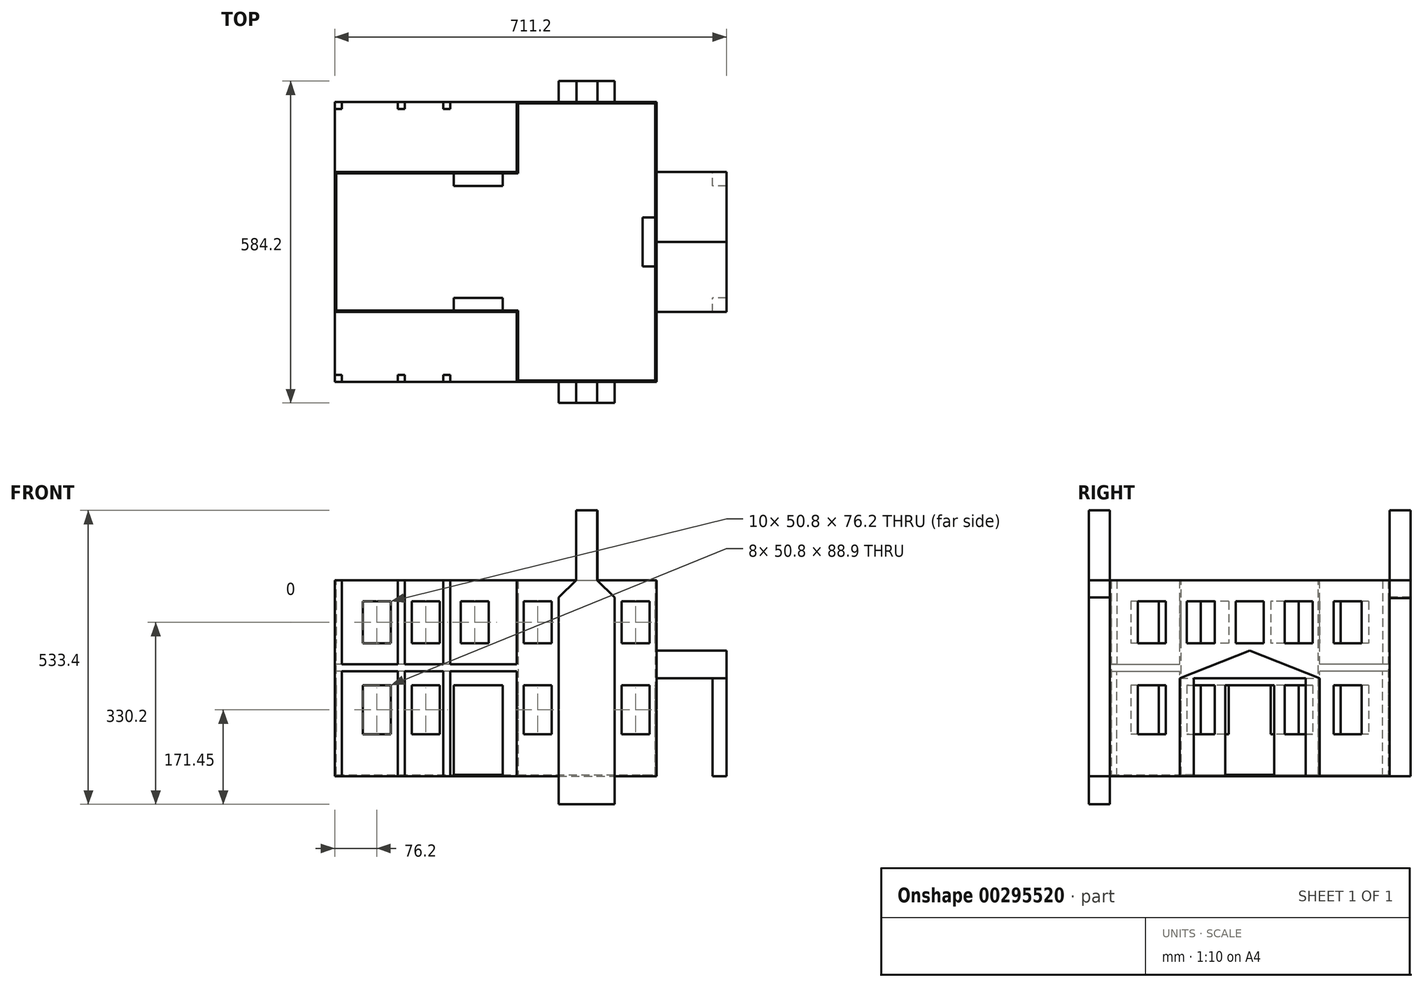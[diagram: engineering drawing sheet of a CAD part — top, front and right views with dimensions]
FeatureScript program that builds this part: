
annotation { "Feature Type Name" : "Feature", "Feature Type Description" : "" }
export const myFeature = defineFeature(function(context is Context, id is Id, definition is map)
    precondition{}
    {
        {
            var Q0;
            Q0=qCreatedBy(makeId("Top.planeOp"),FACE);
            var sketch = newSketch(context, id + "F0", { "sketchPlane" : qUnion([Q0])});
            skLineSegment(sketch, "E0.bottom", {"start": v(0, 0) * mm, "end": v(254, 0) * mm});
            skLineSegment(sketch, "E0.top", {"start": v(0, 508) * mm, "end": v(254, 508) * mm});
            skLineSegment(sketch, "E0.left", {"start": v(0, 0) * mm, "end": v(0, 508) * mm});
            skLineSegment(sketch, "E0.right", {"start": v(254, 0) * mm, "end": v(254, 508) * mm});
            skSolve(sketch);
        }
        {
            var Q0;
            Q0 = qSketchRegion(id + "F0", true);
            extrude(context, id + "F1", {"entities" : qUnion([Q0]), "depth" : 355.6 * mm});
        }
        {
            var Q0;
            Q0=makeQuery(id+"F1.opExtrude","SWEPT_FACE",FACE,{"disambiguationData":[OSD([sQuery(id+"F0.wireOp",EDGE,"E0.left")])]});
            var sketch = newSketch(context, id + "F2", { "sketchPlane" : qUnion([Q0])});
            skLineSegment(sketch, "E1.bottom", {"start": v(-381, 0) * mm, "end": v(-127, 0) * mm});
            skLineSegment(sketch, "E1.top", {"start": v(-381, 355.6) * mm, "end": v(-127, 355.6) * mm});
            skLineSegment(sketch, "E1.left", {"start": v(-381, 0) * mm, "end": v(-381, 355.6) * mm});
            skLineSegment(sketch, "E1.right", {"start": v(-127, 0) * mm, "end": v(-127, 355.6) * mm});
            skSolve(sketch);
        }
        {
            var Q0;
            Q0 = qSketchRegion(id + "F2", true);
            extrude(context, id + "F3", {"entities" : qUnion([Q0]), "operationType" : NewBodyOperationType.ADD, "depth" : 330.2 * mm});
        }
        {
            var Q0;
            Q0=makeQuery(id+"F3.boolean.opBoolean","MERGE",FACE,{"derivedFrom":[makeQuery(id+"F1.opExtrude","CAP_FACE",FACE,{"disambiguationData":[OSD([sQuery(id+"F0.wireOp",EDGE,"E0.bottom"),sQuery(id+"F0.wireOp",EDGE,"E0.top"),sQuery(id+"F0.wireOp",EDGE,"E0.left"),sQuery(id+"F0.wireOp",EDGE,"E0.right")])],"isStart":false}),makeQuery(id+"F3.opExtrude","SWEPT_FACE",FACE,{"disambiguationData":[OSD([sQuery(id+"F2.wireOp",EDGE,"E1.top")])]})]});
            shell(context, id + "F4", {"entities" : qUnion([Q0]), "thickness" : 2.54 * mm});
        }
        {
            var Q0;
            Q0=makeQuery(id+"F1.opExtrude","SWEPT_FACE",FACE,{"disambiguationData":[OSD([sQuery(id+"F0.wireOp",EDGE,"E0.right")])]});
            var sketch = newSketch(context, id + "F5", { "sketchPlane" : qUnion([Q0])});
            skLineSegment(sketch, "E2.bottom", {"start": v(50.8, 317.5) * mm, "end": v(101.6, 317.5) * mm});
            skLineSegment(sketch, "E2.top", {"start": v(50.8, 241.3) * mm, "end": v(101.6, 241.3) * mm});
            skLineSegment(sketch, "E2.left", {"start": v(50.8, 317.5) * mm, "end": v(50.8, 241.3) * mm});
            skLineSegment(sketch, "E2.right", {"start": v(101.6, 317.5) * mm, "end": v(101.6, 241.3) * mm});
            skLineSegment(sketch, "E3.bottom", {"start": v(139.7, 317.5) * mm, "end": v(190.5, 317.5) * mm});
            skLineSegment(sketch, "E3.top", {"start": v(139.7, 241.3) * mm, "end": v(190.5, 241.3) * mm});
            skLineSegment(sketch, "E3.left", {"start": v(139.7, 317.5) * mm, "end": v(139.7, 241.3) * mm});
            skLineSegment(sketch, "E3.right", {"start": v(190.5, 317.5) * mm, "end": v(190.5, 241.3) * mm});
            skLineSegment(sketch, "E4.bottom", {"start": v(228.6, 317.5) * mm, "end": v(279.4, 317.5) * mm});
            skLineSegment(sketch, "E4.top", {"start": v(228.6, 241.3) * mm, "end": v(279.4, 241.3) * mm});
            skLineSegment(sketch, "E4.left", {"start": v(228.6, 317.5) * mm, "end": v(228.6, 241.3) * mm});
            skLineSegment(sketch, "E4.right", {"start": v(279.4, 317.5) * mm, "end": v(279.4, 241.3) * mm});
            skLineSegment(sketch, "E5.bottom", {"start": v(317.5, 317.5) * mm, "end": v(368.3, 317.5) * mm});
            skLineSegment(sketch, "E5.top", {"start": v(317.5, 241.3) * mm, "end": v(368.3, 241.3) * mm});
            skLineSegment(sketch, "E5.left", {"start": v(317.5, 317.5) * mm, "end": v(317.5, 241.3) * mm});
            skLineSegment(sketch, "E5.right", {"start": v(368.3, 317.5) * mm, "end": v(368.3, 241.3) * mm});
            skLineSegment(sketch, "E6.bottom", {"start": v(406.4, 317.5) * mm, "end": v(457.2, 317.5) * mm});
            skLineSegment(sketch, "E6.top", {"start": v(406.4, 241.3) * mm, "end": v(457.2, 241.3) * mm});
            skLineSegment(sketch, "E6.left", {"start": v(406.4, 317.5) * mm, "end": v(406.4, 241.3) * mm});
            skLineSegment(sketch, "E6.right", {"start": v(457.2, 317.5) * mm, "end": v(457.2, 241.3) * mm});
            skPoint(sketch, "E7.endSnap0", {"position": v(254, 317.5) * mm});
            skSolve(sketch);
        }
        {
            var Q0;
            Q0 = qSketchRegion(id + "F5", true);
            extrude(context, id + "F6", {"entities" : qUnion([Q0]), "operationType" : NewBodyOperationType.REMOVE, "oppositeDirection" : true, "depth" : 25.4 * mm});
        }
        {
            var Q0;
            Q0=makeQuery(id+"F1.opExtrude","SWEPT_FACE",FACE,{"disambiguationData":[OSD([sQuery(id+"F0.wireOp",EDGE,"E0.right")])]});
            var sketch = newSketch(context, id + "F7", { "sketchPlane" : qUnion([Q0])});
            skLineSegment(sketch, "E8", {"start": v(254, 228.44) * mm, "end": v(381, 177.8) * mm});
            skLineSegment(sketch, "E9", {"start": v(127, 177.8) * mm, "end": v(381, 177.8) * mm});
            skLineSegment(sketch, "E10", {"start": v(127, 177.8) * mm, "end": v(254, 228.44) * mm});
            skSolve(sketch);
        }
        {
            var Q0;
            Q0=makeQuery(id+"F1.opExtrude","SWEPT_FACE",FACE,{"disambiguationData":[OSD([sQuery(id+"F0.wireOp",EDGE,"E0.right")])]});
            var sketch = newSketch(context, id + "F8", { "sketchPlane" : qUnion([Q0])});
            skLineSegment(sketch, "E11.bottom", {"start": v(50.8, 165.1) * mm, "end": v(101.6, 165.1) * mm});
            skLineSegment(sketch, "E11.top", {"start": v(50.8, 76.2) * mm, "end": v(101.6, 76.2) * mm});
            skLineSegment(sketch, "E11.left", {"start": v(50.8, 165.1) * mm, "end": v(50.8, 76.2) * mm});
            skLineSegment(sketch, "E11.right", {"start": v(101.6, 165.1) * mm, "end": v(101.6, 76.2) * mm});
            skLineSegment(sketch, "E12.bottom", {"start": v(139.7, 165.1) * mm, "end": v(190.5, 165.1) * mm});
            skLineSegment(sketch, "E12.top", {"start": v(139.7, 76.2) * mm, "end": v(190.5, 76.2) * mm});
            skLineSegment(sketch, "E12.left", {"start": v(139.7, 165.1) * mm, "end": v(139.7, 76.2) * mm});
            skLineSegment(sketch, "E12.right", {"start": v(190.5, 165.1) * mm, "end": v(190.5, 76.2) * mm});
            skLineSegment(sketch, "E13.bottom", {"start": v(406.4, 165.1) * mm, "end": v(457.2, 165.1) * mm});
            skLineSegment(sketch, "E13.top", {"start": v(406.4, 76.2) * mm, "end": v(457.2, 76.2) * mm});
            skLineSegment(sketch, "E13.left", {"start": v(406.4, 165.1) * mm, "end": v(406.4, 76.2) * mm});
            skLineSegment(sketch, "E13.right", {"start": v(457.2, 165.1) * mm, "end": v(457.2, 76.2) * mm});
            skLineSegment(sketch, "E14.bottom", {"start": v(317.5, 165.1) * mm, "end": v(368.3, 165.1) * mm});
            skLineSegment(sketch, "E14.top", {"start": v(317.5, 76.2) * mm, "end": v(368.3, 76.2) * mm});
            skLineSegment(sketch, "E14.left", {"start": v(317.5, 165.1) * mm, "end": v(317.5, 76.2) * mm});
            skLineSegment(sketch, "E14.right", {"start": v(368.3, 165.1) * mm, "end": v(368.3, 76.2) * mm});
            skLineSegment(sketch, "E15.bottom", {"start": v(209.55, 165.1) * mm, "end": v(298.45, 165.1) * mm});
            skLineSegment(sketch, "E15.top", {"start": v(209.55, 0) * mm, "end": v(298.45, 0) * mm});
            skLineSegment(sketch, "E15.left", {"start": v(209.55, 165.1) * mm, "end": v(209.55, 0) * mm});
            skLineSegment(sketch, "E15.right", {"start": v(298.45, 165.1) * mm, "end": v(298.45, 0) * mm});
            skSolve(sketch);
        }
        {
            var Q0;
            Q0=makeQuery(id+"F7.imprint","IMPRINT",FACE,{"disambiguationData":[TD([[makeQuery(id+"F7.imprint","IMPRINT",EDGE,{"derivedFrom":sQuery(id+"F7.wireOp",EDGE,"E8")}),-1.0]])]});
            extrude(context, id + "F9", {"entities" : qUnion([Q0]), "operationType" : NewBodyOperationType.ADD, "depth" : 127 * mm});
        }
        {
            var Q0;
            Q0=makeQuery(id+"F9.opExtrude","SWEPT_FACE",FACE,{"disambiguationData":[OSD([sQuery(id+"F7.wireOp",EDGE,"E9")])]});
            var sketch = newSketch(context, id + "F10", { "sketchPlane" : qUnion([Q0])});
            skLineSegment(sketch, "E16.bottom", {"start": v(381, -127) * mm, "end": v(355.6, -127) * mm});
            skLineSegment(sketch, "E16.top", {"start": v(381, -152.4) * mm, "end": v(355.6, -152.4) * mm});
            skLineSegment(sketch, "E16.left", {"start": v(381, -127) * mm, "end": v(381, -152.4) * mm});
            skLineSegment(sketch, "E16.right", {"start": v(355.6, -127) * mm, "end": v(355.6, -152.4) * mm});
            skLineSegment(sketch, "E17.bottom", {"start": v(381, -355.6) * mm, "end": v(355.6, -355.6) * mm});
            skLineSegment(sketch, "E17.top", {"start": v(381, -381) * mm, "end": v(355.6, -381) * mm});
            skLineSegment(sketch, "E17.left", {"start": v(381, -355.6) * mm, "end": v(381, -381) * mm});
            skLineSegment(sketch, "E17.right", {"start": v(355.6, -355.6) * mm, "end": v(355.6, -381) * mm});
            skSolve(sketch);
        }
        {
            var Q0;
            Q0=makeQuery(id+"F10.imprint","IMPRINT",FACE,{"disambiguationData":[TD([[makeQuery(id+"F10.imprint","IMPRINT",EDGE,{"derivedFrom":sQuery(id+"F10.wireOp",EDGE,"E16.bottom")}),1.0]])]});
            var Q1;
            Q1=makeQuery(id+"F10.imprint","IMPRINT",FACE,{"disambiguationData":[TD([[makeQuery(id+"F10.imprint","IMPRINT",EDGE,{"derivedFrom":sQuery(id+"F10.wireOp",EDGE,"E17.bottom")}),1.0]])]});
            extrude(context, id + "F11", {"entities" : qUnion([Q0, Q1]), "operationType" : NewBodyOperationType.ADD, "depth" : 177.8 * mm});
        }
        {
            var Q0;
            Q0=makeQuery(id+"F8.imprint","IMPRINT",FACE,{"disambiguationData":[TD([[makeQuery(id+"F8.imprint","IMPRINT",EDGE,{"derivedFrom":sQuery(id+"F8.wireOp",EDGE,"E11.bottom")}),-1.0]])]});
            var Q1;
            Q1=makeQuery(id+"F8.imprint","IMPRINT",FACE,{"disambiguationData":[TD([[makeQuery(id+"F8.imprint","IMPRINT",EDGE,{"derivedFrom":sQuery(id+"F8.wireOp",EDGE,"E12.bottom")}),-1.0]])]});
            var Q2;
            Q2=makeQuery(id+"F8.imprint","IMPRINT",FACE,{"disambiguationData":[TD([[makeQuery(id+"F8.imprint","IMPRINT",EDGE,{"derivedFrom":sQuery(id+"F8.wireOp",EDGE,"E15.bottom")}),-1.0]])]});
            var Q3;
            Q3=makeQuery(id+"F8.imprint","IMPRINT",FACE,{"disambiguationData":[TD([[makeQuery(id+"F8.imprint","IMPRINT",EDGE,{"derivedFrom":sQuery(id+"F8.wireOp",EDGE,"E14.bottom")}),-1.0]])]});
            var Q4;
            Q4=makeQuery(id+"F8.imprint","IMPRINT",FACE,{"disambiguationData":[TD([[makeQuery(id+"F8.imprint","IMPRINT",EDGE,{"derivedFrom":sQuery(id+"F8.wireOp",EDGE,"E13.bottom")}),-1.0]])]});
            extrude(context, id + "F12", {"entities" : qUnion([Q0, Q1, Q2, Q3, Q4]), "operationType" : NewBodyOperationType.REMOVE, "oppositeDirection" : true, "depth" : 25.4 * mm});
        }
        {
            var Q0;
            Q0=makeQuery(id+"F1.opExtrude","SWEPT_FACE",FACE,{"disambiguationData":[OSD([sQuery(id+"F0.wireOp",EDGE,"E0.right")])]});
            var sketch = newSketch(context, id + "F13", { "sketchPlane" : qUnion([Q0])});
            skLineSegment(sketch, "E18.bottom", {"start": v(209.55, 165.1) * mm, "end": v(298.45, 165.1) * mm});
            skLineSegment(sketch, "E18.top", {"start": v(209.55, 0) * mm, "end": v(298.45, 0) * mm});
            skLineSegment(sketch, "E18.left", {"start": v(209.55, 165.1) * mm, "end": v(209.55, 0) * mm});
            skLineSegment(sketch, "E18.right", {"start": v(298.45, 165.1) * mm, "end": v(298.45, 0) * mm});
            skSolve(sketch);
        }
        {
            var Q0;
            Q0=makeQuery(id+"F1.opExtrude","SWEPT_FACE",FACE,{"disambiguationData":[OSD([sQuery(id+"F0.wireOp",EDGE,"E0.bottom")])]});
            var sketch = newSketch(context, id + "F14", { "sketchPlane" : qUnion([Q0])});
            skLineSegment(sketch, "E19", {"start": v(76.2, 0) * mm, "end": v(76.2, 324.5) * mm});
            skLineSegment(sketch, "E20", {"start": v(177.8, 0) * mm, "end": v(177.8, 324.5) * mm});
            skLineSegment(sketch, "E21", {"start": v(76.2, 324.5) * mm, "end": v(107.95, 355.6) * mm});
            skLineSegment(sketch, "E22", {"start": v(177.8, 324.5) * mm, "end": v(146.05, 355.6) * mm});
            skLineSegment(sketch, "E23", {"start": v(146.05, 355.6) * mm, "end": v(146.05, 482.6) * mm});
            skLineSegment(sketch, "E24", {"start": v(107.95, 355.6) * mm, "end": v(107.95, 482.6) * mm});
            skLineSegment(sketch, "E25", {"start": v(107.95, 482.6) * mm, "end": v(146.05, 482.6) * mm});
            skLineSegment(sketch, "E26.top", {"start": v(76.2, -50.8) * mm, "end": v(177.79, -50.8) * mm});
            skLineSegment(sketch, "E26.left", {"start": v(76.2, 0) * mm, "end": v(76.2, -50.8) * mm});
            skLineSegment(sketch, "E26.right", {"start": v(177.79, 0) * mm, "end": v(177.79, -50.8) * mm});
            skSolve(sketch);
        }
        {
            var Q0;
            {var subQ2=sQuery(id+"F14.wireOp",EDGE,"E19");Q0=makeQuery(id+"F14.imprint","IMPRINT",FACE,{"disambiguationData":[TD([[makeQuery(id+"F14.imprint","IMPRINT",EDGE,{"derivedFrom":subQ2}),-1.0]])]});}
            var Q1;
            {var subQ0=sQuery(id+"F14.wireOp",EDGE,"E25");Q1=makeQuery(id+"F14.imprint","IMPRINT",FACE,{"disambiguationData":[TD([[makeQuery(id+"F14.imprint","IMPRINT",EDGE,{"derivedFrom":subQ0}),-1.0]])]});}
            var Q2;
            Q2=makeQuery(id+"F14.imprint","IMPRINT",FACE,{"disambiguationData":[TD([[makeQuery(id+"F14.imprint","IMPRINT",EDGE,{"derivedFrom":sQuery(id+"F14.wireOp",EDGE,"E26.top")}),1.0]])]});
            extrude(context, id + "F15", {"entities" : qUnion([Q0, Q1, Q2]), "operationType" : NewBodyOperationType.ADD, "depth" : 38.1 * mm});
        }
        {
            var Q0;
            Q0=makeQuery(id+"F1.opExtrude","SWEPT_FACE",FACE,{"disambiguationData":[OSD([sQuery(id+"F0.wireOp",EDGE,"E0.top")])]});
            var sketch = newSketch(context, id + "F16", { "sketchPlane" : qUnion([Q0])});
            skLineSegment(sketch, "E27", {"start": v(-177.8, 0) * mm, "end": v(-177.8, 323.73) * mm});
            skLineSegment(sketch, "E28", {"start": v(-177.8, 323.73) * mm, "end": v(-146.8, 355.6) * mm});
            skLineSegment(sketch, "E29", {"start": v(-146.8, 355.6) * mm, "end": v(-146.8, 482.6) * mm});
            skLineSegment(sketch, "E30", {"start": v(-146.8, 482.6) * mm, "end": v(-108.7, 482.6) * mm});
            skLineSegment(sketch, "E31", {"start": v(-108.7, 482.6) * mm, "end": v(-108.7, 355.6) * mm});
            skLineSegment(sketch, "E32", {"start": v(-108.7, 355.6) * mm, "end": v(-76.2, 325.29) * mm});
            skLineSegment(sketch, "E33", {"start": v(-76.2, 325.29) * mm, "end": v(-76.2, 0) * mm});
            skLineSegment(sketch, "E34", {"start": v(-76.2, 0) * mm, "end": v(-177.8, 0) * mm});
            skLineSegment(sketch, "E35.bottom", {"start": v(-177.8, 0) * mm, "end": v(-76.2, 0) * mm});
            skLineSegment(sketch, "E35.top", {"start": v(-177.8, -50.8) * mm, "end": v(-76.2, -50.8) * mm});
            skLineSegment(sketch, "E35.left", {"start": v(-177.8, 0) * mm, "end": v(-177.8, -50.8) * mm});
            skLineSegment(sketch, "E35.right", {"start": v(-76.2, 0) * mm, "end": v(-76.2, -50.8) * mm});
            skSolve(sketch);
        }
        {
            var Q0;
            Q0=makeQuery(id+"F16.imprint","IMPRINT",FACE,{"disambiguationData":[TD([[makeQuery(id+"F16.imprint","IMPRINT",EDGE,{"derivedFrom":sQuery(id+"F16.wireOp",EDGE,"E27")}),-1.0]])]});
            var Q1;
            {var subQ0=sQuery(id+"F16.wireOp",EDGE,"E29");Q1=makeQuery(id+"F16.imprint","IMPRINT",FACE,{"disambiguationData":[TD([[makeQuery(id+"F16.imprint","IMPRINT",EDGE,{"derivedFrom":subQ0}),-1.0]])]});}
            var Q2;
            Q2=makeQuery(id+"F16.imprint","IMPRINT",FACE,{"disambiguationData":[TD([[makeQuery(id+"F16.imprint","IMPRINT",EDGE,{"derivedFrom":sQuery(id+"F16.wireOp",EDGE,"E35.bottom")}),1.0]])]});
            extrude(context, id + "F17", {"entities" : qUnion([Q0, Q1, Q2]), "operationType" : NewBodyOperationType.ADD, "depth" : 38.1 * mm});
        }
        {
            var Q0;
            Q0=makeQuery(id+"F3.opExtrude","SWEPT_FACE",FACE,{"disambiguationData":[OSD([sQuery(id+"F2.wireOp",EDGE,"E1.right")])]});
            var sketch = newSketch(context, id + "F18", { "sketchPlane" : qUnion([Q0])});
            skLineSegment(sketch, "E36.bottom", {"start": v(-279.4, 317.5) * mm, "end": v(-228.6, 317.5) * mm});
            skLineSegment(sketch, "E36.top", {"start": v(-279.4, 241.3) * mm, "end": v(-228.6, 241.3) * mm});
            skLineSegment(sketch, "E36.left", {"start": v(-279.4, 317.5) * mm, "end": v(-279.4, 241.3) * mm});
            skLineSegment(sketch, "E36.right", {"start": v(-228.6, 317.5) * mm, "end": v(-228.6, 241.3) * mm});
            skLineSegment(sketch, "E37.bottom", {"start": v(-190.5, 317.5) * mm, "end": v(-139.7, 317.5) * mm});
            skLineSegment(sketch, "E37.top", {"start": v(-190.5, 241.3) * mm, "end": v(-139.7, 241.3) * mm});
            skLineSegment(sketch, "E37.left", {"start": v(-190.5, 317.5) * mm, "end": v(-190.5, 241.3) * mm});
            skLineSegment(sketch, "E37.right", {"start": v(-139.7, 317.5) * mm, "end": v(-139.7, 241.3) * mm});
            skLineSegment(sketch, "E38.bottom", {"start": v(-101.6, 317.5) * mm, "end": v(-50.8, 317.5) * mm});
            skLineSegment(sketch, "E38.top", {"start": v(-101.6, 241.3) * mm, "end": v(-50.8, 241.3) * mm});
            skLineSegment(sketch, "E38.left", {"start": v(-101.6, 317.5) * mm, "end": v(-101.6, 241.3) * mm});
            skLineSegment(sketch, "E38.right", {"start": v(-50.8, 317.5) * mm, "end": v(-50.8, 241.3) * mm});
            skLineSegment(sketch, "E39.bottom", {"start": v(-279.4, 165.1) * mm, "end": v(-228.6, 165.1) * mm});
            skLineSegment(sketch, "E39.top", {"start": v(-279.4, 76.2) * mm, "end": v(-228.6, 76.2) * mm});
            skLineSegment(sketch, "E39.left", {"start": v(-279.4, 165.1) * mm, "end": v(-279.4, 76.2) * mm});
            skLineSegment(sketch, "E39.right", {"start": v(-228.6, 165.1) * mm, "end": v(-228.6, 76.2) * mm});
            skLineSegment(sketch, "E40.bottom", {"start": v(-190.5, 165.1) * mm, "end": v(-139.7, 165.1) * mm});
            skLineSegment(sketch, "E40.top", {"start": v(-190.5, 76.2) * mm, "end": v(-139.7, 76.2) * mm});
            skLineSegment(sketch, "E40.left", {"start": v(-190.5, 165.1) * mm, "end": v(-190.5, 76.2) * mm});
            skLineSegment(sketch, "E40.right", {"start": v(-139.7, 165.1) * mm, "end": v(-139.7, 76.2) * mm});
            skSolve(sketch);
        }
        {
            var Q0;
            Q0=makeQuery(id+"F18.imprint","IMPRINT",FACE,{"disambiguationData":[TD([[makeQuery(id+"F18.imprint","IMPRINT",EDGE,{"derivedFrom":sQuery(id+"F18.wireOp",EDGE,"E36.bottom")}),-1.0]])]});
            var Q1;
            Q1=makeQuery(id+"F18.imprint","IMPRINT",FACE,{"disambiguationData":[TD([[makeQuery(id+"F18.imprint","IMPRINT",EDGE,{"derivedFrom":sQuery(id+"F18.wireOp",EDGE,"E37.bottom")}),-1.0]])]});
            var Q2;
            Q2=makeQuery(id+"F18.imprint","IMPRINT",FACE,{"disambiguationData":[TD([[makeQuery(id+"F18.imprint","IMPRINT",EDGE,{"derivedFrom":sQuery(id+"F18.wireOp",EDGE,"E38.bottom")}),-1.0]])]});
            var Q3;
            Q3=makeQuery(id+"F18.imprint","IMPRINT",FACE,{"disambiguationData":[TD([[makeQuery(id+"F18.imprint","IMPRINT",EDGE,{"derivedFrom":sQuery(id+"F18.wireOp",EDGE,"E40.bottom")}),-1.0]])]});
            var Q4;
            Q4=makeQuery(id+"F18.imprint","IMPRINT",FACE,{"disambiguationData":[TD([[makeQuery(id+"F18.imprint","IMPRINT",EDGE,{"derivedFrom":sQuery(id+"F18.wireOp",EDGE,"E39.bottom")}),-1.0]])]});
            extrude(context, id + "F19", {"entities" : qUnion([Q0, Q1, Q2, Q3, Q4]), "operationType" : NewBodyOperationType.REMOVE, "oppositeDirection" : true, "depth" : 25.4 * mm});
        }
        {
            var Q0;
            Q0=makeQuery(id+"F3.opExtrude","SWEPT_FACE",FACE,{"disambiguationData":[OSD([sQuery(id+"F2.wireOp",EDGE,"E1.right")])]});
            var sketch = newSketch(context, id + "F20", { "sketchPlane" : qUnion([Q0])});
            skLineSegment(sketch, "E41.bottom", {"start": v(-114.3, 165.1) * mm, "end": v(-25.4, 165.1) * mm});
            skLineSegment(sketch, "E41.top", {"start": v(-114.3, 0) * mm, "end": v(-25.4, 0) * mm});
            skLineSegment(sketch, "E41.left", {"start": v(-114.3, 165.1) * mm, "end": v(-114.3, 0) * mm});
            skLineSegment(sketch, "E41.right", {"start": v(-25.4, 165.1) * mm, "end": v(-25.4, 0) * mm});
            skSolve(sketch);
        }
        {
            var Q0;
            Q0=makeQuery(id+"F20.imprint","IMPRINT",FACE,{"disambiguationData":[TD([[makeQuery(id+"F20.imprint","IMPRINT",EDGE,{"derivedFrom":sQuery(id+"F20.wireOp",EDGE,"E41.bottom")}),-1.0]])]});
            extrude(context, id + "F21", {"entities" : qUnion([Q0]), "operationType" : NewBodyOperationType.REMOVE, "oppositeDirection" : true, "depth" : 25.4 * mm});
        }
        {
            var Q0;
            Q0=makeQuery(id+"F3.opExtrude","CAP_FACE",FACE,{"disambiguationData":[OSD([sQuery(id+"F2.wireOp",EDGE,"E1.bottom"),sQuery(id+"F2.wireOp",EDGE,"E1.top"),sQuery(id+"F2.wireOp",EDGE,"E1.left"),sQuery(id+"F2.wireOp",EDGE,"E1.right")])],"isStart":false});
            var sketch = newSketch(context, id + "F22", { "sketchPlane" : qUnion([Q0])});
            skLineSegment(sketch, "E42.bottom", {"start": v(-342.9, 317.5) * mm, "end": v(-292.1, 317.5) * mm});
            skLineSegment(sketch, "E42.top", {"start": v(-342.9, 241.3) * mm, "end": v(-292.1, 241.3) * mm});
            skLineSegment(sketch, "E42.left", {"start": v(-342.9, 317.5) * mm, "end": v(-342.9, 241.3) * mm});
            skLineSegment(sketch, "E42.right", {"start": v(-292.1, 317.5) * mm, "end": v(-292.1, 241.3) * mm});
            skLineSegment(sketch, "E43.bottom", {"start": v(-215.9, 317.5) * mm, "end": v(-165.1, 317.5) * mm});
            skLineSegment(sketch, "E43.top", {"start": v(-215.9, 241.3) * mm, "end": v(-165.1, 241.3) * mm});
            skLineSegment(sketch, "E43.left", {"start": v(-215.9, 317.5) * mm, "end": v(-215.9, 241.3) * mm});
            skLineSegment(sketch, "E43.right", {"start": v(-165.1, 317.5) * mm, "end": v(-165.1, 241.3) * mm});
            skLineSegment(sketch, "E44.bottom", {"start": v(-342.9, 165.1) * mm, "end": v(-292.1, 165.1) * mm});
            skLineSegment(sketch, "E44.top", {"start": v(-342.9, 76.2) * mm, "end": v(-292.1, 76.2) * mm});
            skLineSegment(sketch, "E44.left", {"start": v(-342.9, 165.1) * mm, "end": v(-342.9, 76.2) * mm});
            skLineSegment(sketch, "E44.right", {"start": v(-292.1, 165.1) * mm, "end": v(-292.1, 76.2) * mm});
            skLineSegment(sketch, "E45.bottom", {"start": v(-215.9, 165.1) * mm, "end": v(-165.1, 165.1) * mm});
            skLineSegment(sketch, "E45.top", {"start": v(-215.9, 76.2) * mm, "end": v(-165.1, 76.2) * mm});
            skLineSegment(sketch, "E45.left", {"start": v(-215.9, 165.1) * mm, "end": v(-215.9, 76.2) * mm});
            skLineSegment(sketch, "E45.right", {"start": v(-165.1, 165.1) * mm, "end": v(-165.1, 76.2) * mm});
            skSolve(sketch);
        }
        {
            var Q0;
            Q0=makeQuery(id+"F22.imprint","IMPRINT",FACE,{"disambiguationData":[TD([[makeQuery(id+"F22.imprint","IMPRINT",EDGE,{"derivedFrom":sQuery(id+"F22.wireOp",EDGE,"E42.bottom")}),-1.0]])]});
            var Q1;
            Q1=makeQuery(id+"F22.imprint","IMPRINT",FACE,{"disambiguationData":[TD([[makeQuery(id+"F22.imprint","IMPRINT",EDGE,{"derivedFrom":sQuery(id+"F22.wireOp",EDGE,"E43.bottom")}),-1.0]])]});
            var Q2;
            Q2=makeQuery(id+"F22.imprint","IMPRINT",FACE,{"disambiguationData":[TD([[makeQuery(id+"F22.imprint","IMPRINT",EDGE,{"derivedFrom":sQuery(id+"F22.wireOp",EDGE,"E45.bottom")}),-1.0]])]});
            var Q3;
            Q3=makeQuery(id+"F22.imprint","IMPRINT",FACE,{"disambiguationData":[TD([[makeQuery(id+"F22.imprint","IMPRINT",EDGE,{"derivedFrom":sQuery(id+"F22.wireOp",EDGE,"E44.bottom")}),-1.0]])]});
            extrude(context, id + "F23", {"entities" : qUnion([Q0, Q1, Q2, Q3]), "operationType" : NewBodyOperationType.REMOVE, "oppositeDirection" : true, "depth" : 25.4 * mm});
        }
        {
            var Q0;
            {var subQ0=sQuery(id+"F0.wireOp",EDGE,"E0.right");var subQ3=sQuery(id+"F0.wireOp",EDGE,"E0.bottom");Q0=makeQuery(id+"F15.boolean.opBoolean","SPLIT",FACE,{"disambiguationData":[TD([makeQuery(id+"F1.opExtrude","SWEPT_FACE",FACE,{"disambiguationData":[OSD([subQ0])]})])],"derivedFrom":makeQuery(id+"F1.opExtrude","SWEPT_FACE",FACE,{"disambiguationData":[OSD([subQ3])]})});}
            var sketch = newSketch(context, id + "F24", { "sketchPlane" : qUnion([Q0])});
            skLineSegment(sketch, "E46.bottom", {"start": v(190.5, 317.5) * mm, "end": v(241.3, 317.5) * mm});
            skLineSegment(sketch, "E46.top", {"start": v(190.5, 241.3) * mm, "end": v(241.3, 241.3) * mm});
            skLineSegment(sketch, "E46.left", {"start": v(190.5, 317.5) * mm, "end": v(190.5, 241.3) * mm});
            skLineSegment(sketch, "E46.right", {"start": v(241.3, 317.5) * mm, "end": v(241.3, 241.3) * mm});
            skLineSegment(sketch, "E47.bottom", {"start": v(12.7, 317.5) * mm, "end": v(63.5, 317.5) * mm});
            skLineSegment(sketch, "E47.top", {"start": v(12.7, 241.3) * mm, "end": v(63.5, 241.3) * mm});
            skLineSegment(sketch, "E47.left", {"start": v(12.7, 317.5) * mm, "end": v(12.7, 241.3) * mm});
            skLineSegment(sketch, "E47.right", {"start": v(63.5, 317.5) * mm, "end": v(63.5, 241.3) * mm});
            skLineSegment(sketch, "E48.bottom", {"start": v(12.7, 165.1) * mm, "end": v(63.5, 165.1) * mm});
            skLineSegment(sketch, "E48.top", {"start": v(12.7, 76.2) * mm, "end": v(63.5, 76.2) * mm});
            skLineSegment(sketch, "E48.left", {"start": v(12.7, 165.1) * mm, "end": v(12.7, 76.2) * mm});
            skLineSegment(sketch, "E48.right", {"start": v(63.5, 165.1) * mm, "end": v(63.5, 76.2) * mm});
            skLineSegment(sketch, "E49.bottom", {"start": v(190.5, 165.1) * mm, "end": v(241.3, 165.1) * mm});
            skLineSegment(sketch, "E49.top", {"start": v(190.5, 76.2) * mm, "end": v(241.3, 76.2) * mm});
            skLineSegment(sketch, "E49.left", {"start": v(190.5, 165.1) * mm, "end": v(190.5, 76.2) * mm});
            skLineSegment(sketch, "E49.right", {"start": v(241.3, 165.1) * mm, "end": v(241.3, 76.2) * mm});
            skSolve(sketch);
        }
        {
            var Q0;
            Q0=makeQuery(id+"F24.imprint","IMPRINT",FACE,{"disambiguationData":[TD([[makeQuery(id+"F24.imprint","IMPRINT",EDGE,{"derivedFrom":sQuery(id+"F24.wireOp",EDGE,"E47.bottom")}),-1.0]])]});
            var Q1;
            Q1=makeQuery(id+"F24.imprint","IMPRINT",FACE,{"disambiguationData":[TD([[makeQuery(id+"F24.imprint","IMPRINT",EDGE,{"derivedFrom":sQuery(id+"F24.wireOp",EDGE,"E46.bottom")}),-1.0]])]});
            var Q2;
            Q2=makeQuery(id+"F24.imprint","IMPRINT",FACE,{"disambiguationData":[TD([[makeQuery(id+"F24.imprint","IMPRINT",EDGE,{"derivedFrom":sQuery(id+"F24.wireOp",EDGE,"E49.bottom")}),-1.0]])]});
            var Q3;
            Q3=makeQuery(id+"F24.imprint","IMPRINT",FACE,{"disambiguationData":[TD([[makeQuery(id+"F24.imprint","IMPRINT",EDGE,{"derivedFrom":sQuery(id+"F24.wireOp",EDGE,"E48.bottom")}),-1.0]])]});
            extrude(context, id + "F25", {"entities" : qUnion([Q0, Q1, Q2, Q3]), "operationType" : NewBodyOperationType.REMOVE, "oppositeDirection" : true, "depth" : 25.4 * mm});
        }
        {
            var Q0;
            Q0=makeQuery(id+"F3.opExtrude","SWEPT_FACE",FACE,{"disambiguationData":[OSD([sQuery(id+"F2.wireOp",EDGE,"E1.left")])]});
            var sketch = newSketch(context, id + "F26", { "sketchPlane" : qUnion([Q0])});
            skLineSegment(sketch, "E50.bottom", {"start": v(50.8, 317.5) * mm, "end": v(101.6, 317.5) * mm});
            skLineSegment(sketch, "E50.top", {"start": v(50.8, 241.3) * mm, "end": v(101.6, 241.3) * mm});
            skLineSegment(sketch, "E50.left", {"start": v(50.8, 317.5) * mm, "end": v(50.8, 241.3) * mm});
            skLineSegment(sketch, "E50.right", {"start": v(101.6, 317.5) * mm, "end": v(101.6, 241.3) * mm});
            skLineSegment(sketch, "E51.bottom", {"start": v(139.7, 317.5) * mm, "end": v(190.5, 317.5) * mm});
            skLineSegment(sketch, "E51.top", {"start": v(139.7, 241.3) * mm, "end": v(190.5, 241.3) * mm});
            skLineSegment(sketch, "E51.left", {"start": v(139.7, 317.5) * mm, "end": v(139.7, 241.3) * mm});
            skLineSegment(sketch, "E51.right", {"start": v(190.5, 317.5) * mm, "end": v(190.5, 241.3) * mm});
            skLineSegment(sketch, "E52.bottom", {"start": v(228.6, 317.5) * mm, "end": v(279.4, 317.5) * mm});
            skLineSegment(sketch, "E52.top", {"start": v(228.6, 241.3) * mm, "end": v(279.4, 241.3) * mm});
            skLineSegment(sketch, "E52.left", {"start": v(228.6, 317.5) * mm, "end": v(228.6, 241.3) * mm});
            skLineSegment(sketch, "E52.right", {"start": v(279.4, 317.5) * mm, "end": v(279.4, 241.3) * mm});
            skLineSegment(sketch, "E53.bottom", {"start": v(228.6, 165.1) * mm, "end": v(279.4, 165.1) * mm});
            skLineSegment(sketch, "E53.top", {"start": v(228.6, 76.2) * mm, "end": v(279.4, 76.2) * mm});
            skLineSegment(sketch, "E53.left", {"start": v(228.6, 165.1) * mm, "end": v(228.6, 76.2) * mm});
            skLineSegment(sketch, "E53.right", {"start": v(279.4, 165.1) * mm, "end": v(279.4, 76.2) * mm});
            skLineSegment(sketch, "E54.bottom", {"start": v(139.7, 165.1) * mm, "end": v(190.5, 165.1) * mm});
            skLineSegment(sketch, "E54.top", {"start": v(139.7, 76.2) * mm, "end": v(190.5, 76.2) * mm});
            skLineSegment(sketch, "E54.left", {"start": v(139.7, 165.1) * mm, "end": v(139.7, 76.2) * mm});
            skLineSegment(sketch, "E54.right", {"start": v(190.5, 165.1) * mm, "end": v(190.5, 76.2) * mm});
            skLineSegment(sketch, "E55.bottom", {"start": v(25.4, 165.1) * mm, "end": v(114.3, 165.1) * mm});
            skLineSegment(sketch, "E55.top", {"start": v(25.4, 0) * mm, "end": v(114.3, 0) * mm});
            skLineSegment(sketch, "E55.left", {"start": v(25.4, 165.1) * mm, "end": v(25.4, 0) * mm});
            skLineSegment(sketch, "E55.right", {"start": v(114.3, 165.1) * mm, "end": v(114.3, 0) * mm});
            skSolve(sketch);
        }
        {
            var Q0;
            Q0=makeQuery(id+"F26.imprint","IMPRINT",FACE,{"disambiguationData":[TD([[makeQuery(id+"F26.imprint","IMPRINT",EDGE,{"derivedFrom":sQuery(id+"F26.wireOp",EDGE,"E55.bottom")}),-1.0]])]});
            var Q1;
            Q1=makeQuery(id+"F26.imprint","IMPRINT",FACE,{"disambiguationData":[TD([[makeQuery(id+"F26.imprint","IMPRINT",EDGE,{"derivedFrom":sQuery(id+"F26.wireOp",EDGE,"E54.bottom")}),-1.0]])]});
            var Q2;
            Q2=makeQuery(id+"F26.imprint","IMPRINT",FACE,{"disambiguationData":[TD([[makeQuery(id+"F26.imprint","IMPRINT",EDGE,{"derivedFrom":sQuery(id+"F26.wireOp",EDGE,"E53.bottom")}),-1.0]])]});
            var Q3;
            Q3=makeQuery(id+"F26.imprint","IMPRINT",FACE,{"disambiguationData":[TD([[makeQuery(id+"F26.imprint","IMPRINT",EDGE,{"derivedFrom":sQuery(id+"F26.wireOp",EDGE,"E52.bottom")}),-1.0]])]});
            var Q4;
            Q4=makeQuery(id+"F26.imprint","IMPRINT",FACE,{"disambiguationData":[TD([[makeQuery(id+"F26.imprint","IMPRINT",EDGE,{"derivedFrom":sQuery(id+"F26.wireOp",EDGE,"E51.bottom")}),-1.0]])]});
            var Q5;
            Q5=makeQuery(id+"F26.imprint","IMPRINT",FACE,{"disambiguationData":[TD([[makeQuery(id+"F26.imprint","IMPRINT",EDGE,{"derivedFrom":sQuery(id+"F26.wireOp",EDGE,"E50.bottom")}),-1.0]])]});
            extrude(context, id + "F27", {"entities" : qUnion([Q0, Q1, Q2, Q3, Q4, Q5]), "operationType" : NewBodyOperationType.REMOVE, "oppositeDirection" : true, "depth" : 25.4 * mm});
        }
        {
            var Q0;
            {var subQ1=sQuery(id+"F0.wireOp",EDGE,"E0.left");var subQ2=sQuery(id+"F0.wireOp",EDGE,"E0.top");Q0=makeQuery(id+"F3.boolean.opBoolean","SPLIT",FACE,{"disambiguationData":[TD([makeQuery(id+"F1.opExtrude","SWEPT_FACE",FACE,{"disambiguationData":[OSD([subQ2])]})])],"derivedFrom":makeQuery(id+"F1.opExtrude","SWEPT_FACE",FACE,{"disambiguationData":[OSD([subQ1])]})});}
            var sketch = newSketch(context, id + "F28", { "sketchPlane" : qUnion([Q0])});
            skLineSegment(sketch, "E56.bottom", {"start": v(-469.9, 317.5) * mm, "end": v(-419.1, 317.5) * mm});
            skLineSegment(sketch, "E56.top", {"start": v(-469.9, 241.3) * mm, "end": v(-419.1, 241.3) * mm});
            skLineSegment(sketch, "E56.left", {"start": v(-469.9, 317.5) * mm, "end": v(-469.9, 241.3) * mm});
            skLineSegment(sketch, "E56.right", {"start": v(-419.1, 317.5) * mm, "end": v(-419.1, 241.3) * mm});
            skLineSegment(sketch, "E57.bottom", {"start": v(-469.9, 165.1) * mm, "end": v(-419.1, 165.1) * mm});
            skLineSegment(sketch, "E57.top", {"start": v(-469.9, 76.2) * mm, "end": v(-419.1, 76.2) * mm});
            skLineSegment(sketch, "E57.left", {"start": v(-469.9, 165.1) * mm, "end": v(-469.9, 76.2) * mm});
            skLineSegment(sketch, "E57.right", {"start": v(-419.1, 165.1) * mm, "end": v(-419.1, 76.2) * mm});
            skLineSegment(sketch, "E58.bottom", {"start": v(-88.9, 317.5) * mm, "end": v(-38.1, 317.5) * mm});
            skLineSegment(sketch, "E58.top", {"start": v(-88.9, 241.3) * mm, "end": v(-38.1, 241.3) * mm});
            skLineSegment(sketch, "E58.left", {"start": v(-88.9, 317.5) * mm, "end": v(-88.9, 241.3) * mm});
            skLineSegment(sketch, "E58.right", {"start": v(-38.1, 317.5) * mm, "end": v(-38.1, 241.3) * mm});
            skLineSegment(sketch, "E59.bottom", {"start": v(-88.9, 165.1) * mm, "end": v(-38.1, 165.1) * mm});
            skLineSegment(sketch, "E59.top", {"start": v(-88.9, 76.2) * mm, "end": v(-38.1, 76.2) * mm});
            skLineSegment(sketch, "E59.left", {"start": v(-88.9, 165.1) * mm, "end": v(-88.9, 76.2) * mm});
            skLineSegment(sketch, "E59.right", {"start": v(-38.1, 165.1) * mm, "end": v(-38.1, 76.2) * mm});
            skSolve(sketch);
        }
        {
            var Q0;
            Q0=makeQuery(id+"F28.imprint","IMPRINT",FACE,{"disambiguationData":[TD([[makeQuery(id+"F28.imprint","IMPRINT",EDGE,{"derivedFrom":sQuery(id+"F28.wireOp",EDGE,"E56.bottom")}),-1.0]])]});
            var Q1;
            Q1=makeQuery(id+"F28.imprint","IMPRINT",FACE,{"disambiguationData":[TD([[makeQuery(id+"F28.imprint","IMPRINT",EDGE,{"derivedFrom":sQuery(id+"F28.wireOp",EDGE,"E57.bottom")}),-1.0]])]});
            var Q2;
            Q2=makeQuery(id+"F28.imprint","IMPRINT",FACE,{"disambiguationData":[TD([[makeQuery(id+"F28.imprint","IMPRINT",EDGE,{"derivedFrom":sQuery(id+"F28.wireOp",EDGE,"E58.bottom")}),-1.0]])]});
            var Q3;
            Q3=makeQuery(id+"F28.imprint","IMPRINT",FACE,{"disambiguationData":[TD([[makeQuery(id+"F28.imprint","IMPRINT",EDGE,{"derivedFrom":sQuery(id+"F28.wireOp",EDGE,"E59.bottom")}),-1.0]])]});
            extrude(context, id + "F29", {"entities" : qUnion([Q0, Q1, Q2, Q3]), "operationType" : NewBodyOperationType.REMOVE, "oppositeDirection" : true, "depth" : 25.4 * mm});
        }
        {
            var Q0;
            {var subQ5=sQuery(id+"F0.wireOp",EDGE,"E0.right");var subQ7=sQuery(id+"F0.wireOp",EDGE,"E0.top");Q0=makeQuery(id+"F17.boolean.opBoolean","SPLIT",FACE,{"disambiguationData":[TD([makeQuery(id+"F1.opExtrude","SWEPT_FACE",FACE,{"disambiguationData":[OSD([subQ5])]})])],"derivedFrom":makeQuery(id+"F1.opExtrude","SWEPT_FACE",FACE,{"disambiguationData":[OSD([subQ7])]})});}
            var sketch = newSketch(context, id + "F30", { "sketchPlane" : qUnion([Q0])});
            skLineSegment(sketch, "E60.bottom", {"start": v(-241.3, 317.5) * mm, "end": v(-190.5, 317.5) * mm});
            skLineSegment(sketch, "E60.top", {"start": v(-241.3, 241.3) * mm, "end": v(-190.5, 241.3) * mm});
            skLineSegment(sketch, "E60.left", {"start": v(-241.3, 317.5) * mm, "end": v(-241.3, 241.3) * mm});
            skLineSegment(sketch, "E60.right", {"start": v(-190.5, 317.5) * mm, "end": v(-190.5, 241.3) * mm});
            skLineSegment(sketch, "E61.bottom", {"start": v(-241.3, 165.1) * mm, "end": v(-190.5, 165.1) * mm});
            skLineSegment(sketch, "E61.top", {"start": v(-241.3, 76.2) * mm, "end": v(-190.5, 76.2) * mm});
            skLineSegment(sketch, "E61.left", {"start": v(-241.3, 165.1) * mm, "end": v(-241.3, 76.2) * mm});
            skLineSegment(sketch, "E61.right", {"start": v(-190.5, 165.1) * mm, "end": v(-190.5, 76.2) * mm});
            skLineSegment(sketch, "E62.bottom", {"start": v(-63.5, 317.5) * mm, "end": v(-12.7, 317.5) * mm});
            skLineSegment(sketch, "E62.top", {"start": v(-63.5, 241.3) * mm, "end": v(-12.7, 241.3) * mm});
            skLineSegment(sketch, "E62.left", {"start": v(-63.5, 317.5) * mm, "end": v(-63.5, 241.3) * mm});
            skLineSegment(sketch, "E62.right", {"start": v(-12.7, 317.5) * mm, "end": v(-12.7, 241.3) * mm});
            skLineSegment(sketch, "E63.bottom", {"start": v(-63.5, 165.1) * mm, "end": v(-12.7, 165.1) * mm});
            skLineSegment(sketch, "E63.top", {"start": v(-63.5, 76.2) * mm, "end": v(-12.7, 76.2) * mm});
            skLineSegment(sketch, "E63.left", {"start": v(-63.5, 165.1) * mm, "end": v(-63.5, 76.2) * mm});
            skLineSegment(sketch, "E63.right", {"start": v(-12.7, 165.1) * mm, "end": v(-12.7, 76.2) * mm});
            skSolve(sketch);
        }
        {
            var Q0;
            Q0=makeQuery(id+"F30.imprint","IMPRINT",FACE,{"disambiguationData":[TD([[makeQuery(id+"F30.imprint","IMPRINT",EDGE,{"derivedFrom":sQuery(id+"F30.wireOp",EDGE,"E60.bottom")}),-1.0]])]});
            var Q1;
            Q1=makeQuery(id+"F30.imprint","IMPRINT",FACE,{"disambiguationData":[TD([[makeQuery(id+"F30.imprint","IMPRINT",EDGE,{"derivedFrom":sQuery(id+"F30.wireOp",EDGE,"E61.bottom")}),-1.0]])]});
            var Q2;
            Q2=makeQuery(id+"F30.imprint","IMPRINT",FACE,{"disambiguationData":[TD([[makeQuery(id+"F30.imprint","IMPRINT",EDGE,{"derivedFrom":sQuery(id+"F30.wireOp",EDGE,"E62.bottom")}),-1.0]])]});
            var Q3;
            Q3=makeQuery(id+"F30.imprint","IMPRINT",FACE,{"disambiguationData":[TD([[makeQuery(id+"F30.imprint","IMPRINT",EDGE,{"derivedFrom":sQuery(id+"F30.wireOp",EDGE,"E63.bottom")}),-1.0]])]});
            extrude(context, id + "F31", {"entities" : qUnion([Q0, Q1, Q2, Q3]), "operationType" : NewBodyOperationType.REMOVE, "oppositeDirection" : true, "depth" : 25.4 * mm});
        }
        {
            var Q0;
            Q0=makeQuery(id+"F3.opExtrude","SWEPT_FACE",FACE,{"disambiguationData":[OSD([sQuery(id+"F2.wireOp",EDGE,"E1.right")])]});
            var sketch = newSketch(context, id + "F32", { "sketchPlane" : qUnion([Q0])});
            skLineSegment(sketch, "E64.bottom", {"start": v(-330.2, 203.2) * mm, "end": v(0, 203.2) * mm});
            skLineSegment(sketch, "E64.top", {"start": v(-330.2, 190.5) * mm, "end": v(0, 190.5) * mm});
            skLineSegment(sketch, "E64.left", {"start": v(-330.2, 203.2) * mm, "end": v(-330.2, 190.5) * mm});
            skLineSegment(sketch, "E64.right", {"start": v(0, 203.2) * mm, "end": v(0, 190.5) * mm});
            skSolve(sketch);
        }
        {
            var Q0;
            Q0 = qSketchRegion(id + "F32", true);
            extrude(context, id + "F33", {"entities" : qUnion([Q0]), "operationType" : NewBodyOperationType.ADD, "depth" : 127 * mm});
        }
        {
            var Q0;
            Q0=makeQuery(id+"F33.opExtrude","SWEPT_FACE",FACE,{"disambiguationData":[OSD([sQuery(id+"F32.wireOp",EDGE,"E64.top")])]});
            var sketch = newSketch(context, id + "F34", { "sketchPlane" : qUnion([Q0])});
            skLineSegment(sketch, "E65.bottom", {"start": v(-330.2, 0) * mm, "end": v(-317.5, 0) * mm});
            skLineSegment(sketch, "E65.top", {"start": v(-330.2, -12.7) * mm, "end": v(-317.5, -12.7) * mm});
            skLineSegment(sketch, "E65.left", {"start": v(-330.2, 0) * mm, "end": v(-330.2, -12.7) * mm});
            skLineSegment(sketch, "E65.right", {"start": v(-317.5, 0) * mm, "end": v(-317.5, -12.7) * mm});
            skLineSegment(sketch, "E66.bottom", {"start": v(-215.9, 0) * mm, "end": v(-203.2, 0) * mm});
            skLineSegment(sketch, "E66.top", {"start": v(-215.9, -12.7) * mm, "end": v(-203.2, -12.7) * mm});
            skLineSegment(sketch, "E66.left", {"start": v(-215.9, 0) * mm, "end": v(-215.9, -12.7) * mm});
            skLineSegment(sketch, "E66.right", {"start": v(-203.2, 0) * mm, "end": v(-203.2, -12.7) * mm});
            skLineSegment(sketch, "E67.bottom", {"start": v(-133.35, 0) * mm, "end": v(-120.65, 0) * mm});
            skLineSegment(sketch, "E67.top", {"start": v(-133.35, -12.7) * mm, "end": v(-120.65, -12.7) * mm});
            skLineSegment(sketch, "E67.left", {"start": v(-133.35, 0) * mm, "end": v(-133.35, -12.7) * mm});
            skLineSegment(sketch, "E67.right", {"start": v(-120.65, 0) * mm, "end": v(-120.65, -12.7) * mm});
            skSolve(sketch);
        }
        {
            var Q0;
            Q0 = qSketchRegion(id + "F34", true);
            extrude(context, id + "F35", {"entities" : qUnion([Q0]), "operationType" : NewBodyOperationType.ADD, "depth" : 190.5 * mm});
        }
        {
            var Q0;
            Q0=makeQuery(id+"F33.opExtrude","SWEPT_FACE",FACE,{"disambiguationData":[OSD([sQuery(id+"F32.wireOp",EDGE,"E64.bottom")])]});
            var sketch = newSketch(context, id + "F36", { "sketchPlane" : qUnion([Q0])});
            skLineSegment(sketch, "E68.bottom", {"start": v(-330.2, 12.7) * mm, "end": v(-317.5, 12.7) * mm});
            skLineSegment(sketch, "E68.top", {"start": v(-330.2, 0) * mm, "end": v(-317.5, 0) * mm});
            skLineSegment(sketch, "E68.left", {"start": v(-330.2, 12.7) * mm, "end": v(-330.2, 0) * mm});
            skLineSegment(sketch, "E68.right", {"start": v(-317.5, 12.7) * mm, "end": v(-317.5, 0) * mm});
            skLineSegment(sketch, "E69.bottom", {"start": v(-215.9, 12.7) * mm, "end": v(-203.2, 12.7) * mm});
            skLineSegment(sketch, "E69.top", {"start": v(-215.9, 0) * mm, "end": v(-203.2, 0) * mm});
            skLineSegment(sketch, "E69.left", {"start": v(-215.9, 12.7) * mm, "end": v(-215.9, 0) * mm});
            skLineSegment(sketch, "E69.right", {"start": v(-203.2, 12.7) * mm, "end": v(-203.2, 0) * mm});
            skLineSegment(sketch, "E70.bottom", {"start": v(-133.35, 12.7) * mm, "end": v(-120.65, 12.7) * mm});
            skLineSegment(sketch, "E70.top", {"start": v(-133.35, 0) * mm, "end": v(-120.65, 0) * mm});
            skLineSegment(sketch, "E70.left", {"start": v(-133.35, 12.7) * mm, "end": v(-133.35, 0) * mm});
            skLineSegment(sketch, "E70.right", {"start": v(-120.65, 12.7) * mm, "end": v(-120.65, 0) * mm});
            skSolve(sketch);
        }
        {
            var Q0;
            Q0 = qSketchRegion(id + "F36", true);
            extrude(context, id + "F37", {"entities" : qUnion([Q0]), "operationType" : NewBodyOperationType.ADD, "depth" : 152.4 * mm});
        }
        {
            var Q0;
            Q0=makeQuery(id+"F3.opExtrude","SWEPT_FACE",FACE,{"disambiguationData":[OSD([sQuery(id+"F2.wireOp",EDGE,"E1.left")])]});
            var sketch = newSketch(context, id + "F38", { "sketchPlane" : qUnion([Q0])});
            skLineSegment(sketch, "E71.bottom", {"start": v(0, 203.2) * mm, "end": v(330.2, 203.2) * mm});
            skLineSegment(sketch, "E71.top", {"start": v(0, 190.5) * mm, "end": v(330.2, 190.5) * mm});
            skLineSegment(sketch, "E71.left", {"start": v(0, 203.2) * mm, "end": v(0, 190.5) * mm});
            skLineSegment(sketch, "E71.right", {"start": v(330.2, 203.2) * mm, "end": v(330.2, 190.5) * mm});
            skSolve(sketch);
        }
        {
            var Q0;
            Q0 = qSketchRegion(id + "F38", true);
            extrude(context, id + "F39", {"entities" : qUnion([Q0]), "operationType" : NewBodyOperationType.ADD, "depth" : 127 * mm});
        }
        {
            var Q0;
            Q0=makeQuery(id+"F39.opExtrude","SWEPT_FACE",FACE,{"disambiguationData":[OSD([sQuery(id+"F38.wireOp",EDGE,"E71.top")])]});
            var sketch = newSketch(context, id + "F40", { "sketchPlane" : qUnion([Q0])});
            skLineSegment(sketch, "E72.bottom", {"start": v(-120.65, -508) * mm, "end": v(-133.35, -508) * mm});
            skLineSegment(sketch, "E72.top", {"start": v(-120.65, -495.3) * mm, "end": v(-133.35, -495.3) * mm});
            skLineSegment(sketch, "E72.left", {"start": v(-120.65, -508) * mm, "end": v(-120.65, -495.3) * mm});
            skLineSegment(sketch, "E72.right", {"start": v(-133.35, -508) * mm, "end": v(-133.35, -495.3) * mm});
            skLineSegment(sketch, "E73.bottom", {"start": v(-203.2, -508) * mm, "end": v(-215.9, -508) * mm});
            skLineSegment(sketch, "E73.top", {"start": v(-203.2, -495.3) * mm, "end": v(-215.9, -495.3) * mm});
            skLineSegment(sketch, "E73.left", {"start": v(-203.2, -508) * mm, "end": v(-203.2, -495.3) * mm});
            skLineSegment(sketch, "E73.right", {"start": v(-215.9, -508) * mm, "end": v(-215.9, -495.3) * mm});
            skLineSegment(sketch, "E74.bottom", {"start": v(-317.5, -508) * mm, "end": v(-330.2, -508) * mm});
            skLineSegment(sketch, "E74.top", {"start": v(-317.5, -495.3) * mm, "end": v(-330.2, -495.3) * mm});
            skLineSegment(sketch, "E74.left", {"start": v(-317.5, -508) * mm, "end": v(-317.5, -495.3) * mm});
            skLineSegment(sketch, "E74.right", {"start": v(-330.2, -508) * mm, "end": v(-330.2, -495.3) * mm});
            skSolve(sketch);
        }
        {
            var Q0;
            Q0 = qSketchRegion(id + "F40", true);
            extrude(context, id + "F41", {"entities" : qUnion([Q0]), "operationType" : NewBodyOperationType.ADD, "depth" : 190.5 * mm});
        }
        {
            var Q0;
            Q0=makeQuery(id+"F39.opExtrude","SWEPT_FACE",FACE,{"disambiguationData":[OSD([sQuery(id+"F38.wireOp",EDGE,"E71.bottom")])]});
            var sketch = newSketch(context, id + "F42", { "sketchPlane" : qUnion([Q0])});
            skLineSegment(sketch, "E75.bottom", {"start": v(-120.65, 508) * mm, "end": v(-133.35, 508) * mm});
            skLineSegment(sketch, "E75.top", {"start": v(-120.65, 495.3) * mm, "end": v(-133.35, 495.3) * mm});
            skLineSegment(sketch, "E75.left", {"start": v(-120.65, 508) * mm, "end": v(-120.65, 495.3) * mm});
            skLineSegment(sketch, "E75.right", {"start": v(-133.35, 508) * mm, "end": v(-133.35, 495.3) * mm});
            skLineSegment(sketch, "E76.bottom", {"start": v(-203.2, 508) * mm, "end": v(-215.9, 508) * mm});
            skLineSegment(sketch, "E76.top", {"start": v(-203.2, 495.3) * mm, "end": v(-215.9, 495.3) * mm});
            skLineSegment(sketch, "E76.left", {"start": v(-203.2, 508) * mm, "end": v(-203.2, 495.3) * mm});
            skLineSegment(sketch, "E76.right", {"start": v(-215.9, 508) * mm, "end": v(-215.9, 495.3) * mm});
            skLineSegment(sketch, "E77.bottom", {"start": v(-317.5, 508) * mm, "end": v(-330.2, 508) * mm});
            skLineSegment(sketch, "E77.top", {"start": v(-317.5, 495.3) * mm, "end": v(-330.2, 495.3) * mm});
            skLineSegment(sketch, "E77.left", {"start": v(-317.5, 508) * mm, "end": v(-317.5, 495.3) * mm});
            skLineSegment(sketch, "E77.right", {"start": v(-330.2, 508) * mm, "end": v(-330.2, 495.3) * mm});
            skSolve(sketch);
        }
        {
            var Q0;
            Q0 = qSketchRegion(id + "F42", true);
            extrude(context, id + "F43", {"entities" : qUnion([Q0]), "operationType" : NewBodyOperationType.ADD, "depth" : 152.4 * mm});
        }
    });
